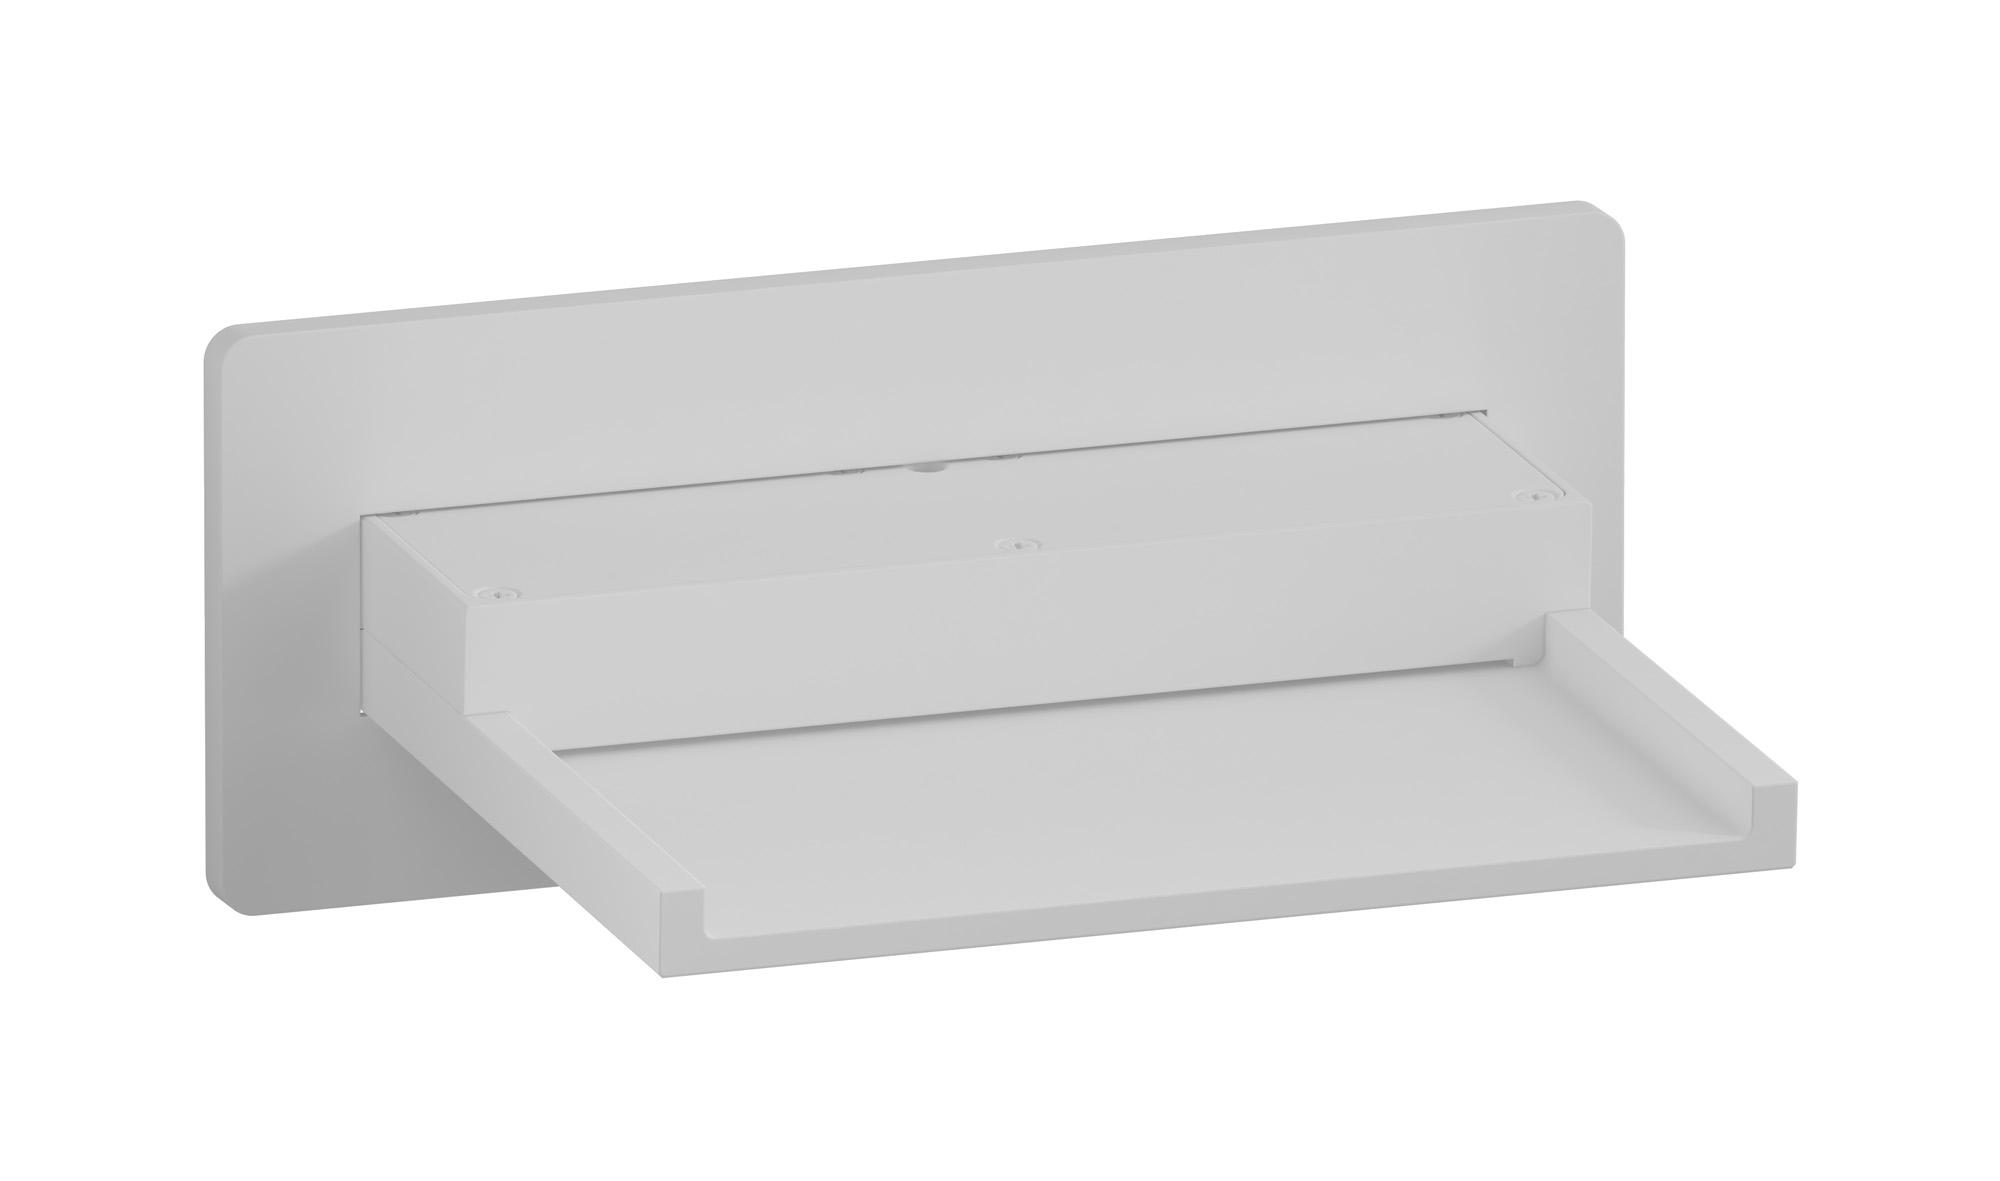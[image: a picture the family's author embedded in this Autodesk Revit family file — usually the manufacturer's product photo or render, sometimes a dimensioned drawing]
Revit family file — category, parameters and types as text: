
# Revit family: RU318
name_source: partatom
category: Apparecchi idraulici
units: mm (PartAtom-declared; Revit-internal decimal feet)

## family parameters
Basato su piano di lavoro = No
Condiviso = No
Mantieni orientamento annotazione = No
Numero OmniClass = 23.45.55.17
Punto di calcolo locali = No
Quota connettore circolare = Usa diametro
Sempre verticale = Sì
Taglio con vuoti quando caricato = No
Tipo di parte = Normale
Titolo OmniClass = Mixing Faucets

## types (12) — shared parameters
Commenti sul tipo = Built in wall mounted waterfall spout
Connessione CW = No
Connessione HW = No
Connessione di scarico = No
Connessione di ventilazione = No
Descrizione = Built in wall mounted waterfall spout
Produttore = IB Rubinetterie S.p.A.
URL = https://www.weareib.it
Water inlet = 10 mm  [stored 0.0328084 ft]
zero-valued in all types: Prospetto di default

## per-type parameters (varying)
| type | Finishes surface | Immagine tipo | Modello |
| Matt White | IB_matt white | RU318BO.jpg | RU318BB |
| Chrome | IB_Chrome | RU318CC.jpg | RU318CC |
| Black Chrome | IB_Black chrome | RU318CF.jpg | RU318CF |
| Brushed Black Chrome | IB_Brushed black chrome | RU318CS.jpg | RU318CS |
| Pale Gold | IB_Pale gold | RU318II.jpg | RU318II |
| Brushed Pale Gold | IB_brushed pale gold | RU318IS.jpg | RU318IS |
| Matt Black | IB_matt black | RU318NP.jpg | RU318NP |
| Gold | IB_gold | RU318OO.jpg | RU318OO |
| Brushed Gold | IB_brushed gold | RU318OS.jpg | RU318OS |
| Rose Gold | IB_Rose gold | RU318RS.jpg | RU318RS |
| Brushed Rose Gold | IB_Brushed rose gold | RU318SR.jpg | RU318SR |
| Brushed Nickel | IB_Brushed nickel | RU318SS.jpg | RU318SS |

note: [stored X ft] marks values corroborated as IEEE doubles in the binary element streams (Revit-internal decimal feet)
